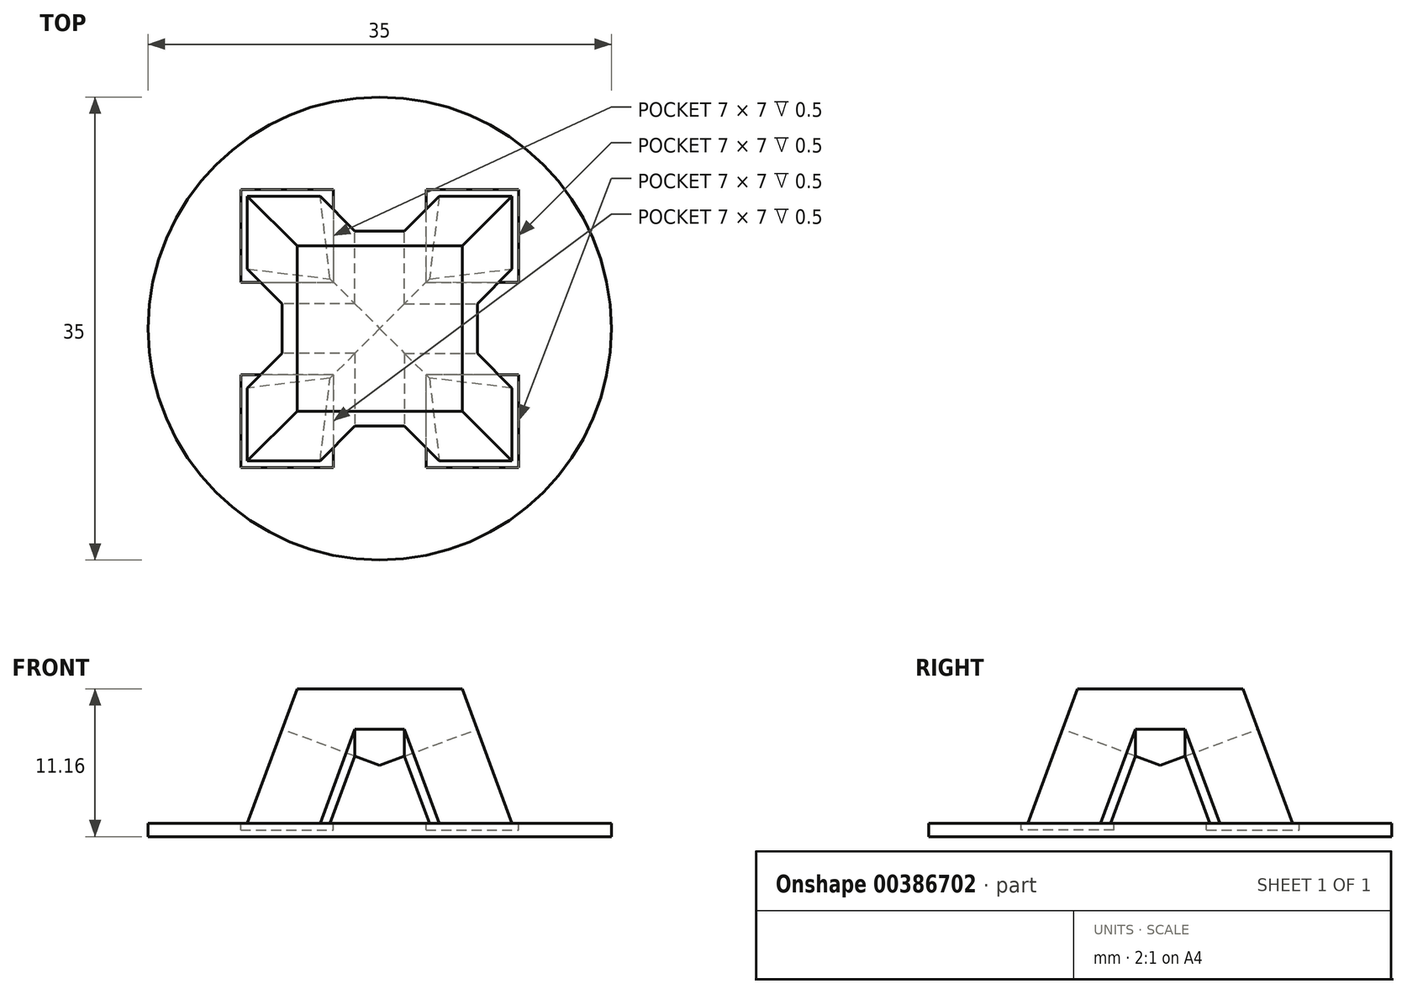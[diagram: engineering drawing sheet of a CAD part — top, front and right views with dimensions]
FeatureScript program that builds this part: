
annotation { "Feature Type Name" : "Feature", "Feature Type Description" : "" }
export const myFeature = defineFeature(function(context is Context, id is Id, definition is map)
    precondition{}
    {
        {
            var Q0;
            Q0=qCreatedBy(makeId("Top.planeOp"),FACE);
            var sketch = newSketch(context, id + "F0", { "sketchPlane" : qUnion([Q0])});
            skLineSegment(sketch, "E0.bottom", {"start": v(-10, 10) * mm, "end": v(10, 10) * mm});
            skLineSegment(sketch, "E0.top", {"start": v(-10, -10) * mm, "end": v(10, -10) * mm});
            skLineSegment(sketch, "E0.left", {"start": v(-10, 10) * mm, "end": v(-10, -10) * mm});
            skLineSegment(sketch, "E0.right", {"start": v(10, 10) * mm, "end": v(10, -10) * mm});
            skPoint(sketch, "E0.middle", {"position": v(0, 0) * mm});
            skSolve(sketch);
        }
        {
            var Q0;
            Q0=qCreatedBy(makeId("Top.planeOp"),FACE);
            cPlane(context, id + "F1", {"entities" : qUnion([Q0]), "cplaneType" : CPlaneType.OFFSET, "offset" : 10.16 * mm, "width" : 150 * mm, "height" : 150 * mm});
        }
        {
            var Q0;
            Q0=qCreatedBy(id+"F1.planeOp",FACE);
            var sketch = newSketch(context, id + "F2", { "sketchPlane" : qUnion([Q0])});
            skLineSegment(sketch, "E1.bottom", {"start": v(-6.25, 6.25) * mm, "end": v(6.25, 6.25) * mm});
            skLineSegment(sketch, "E1.top", {"start": v(-6.25, -6.25) * mm, "end": v(6.25, -6.25) * mm});
            skLineSegment(sketch, "E1.left", {"start": v(-6.25, 6.25) * mm, "end": v(-6.25, -6.25) * mm});
            skLineSegment(sketch, "E1.right", {"start": v(6.25, 6.25) * mm, "end": v(6.25, -6.25) * mm});
            skPoint(sketch, "E1.middle", {"position": v(0, 0) * mm});
            skSolve(sketch);
        }
        {
            var Q0;
            Q0=makeQuery(id+"F0.imprint","IMPRINT",FACE,{"disambiguationData":[TD([[makeQuery(id+"F0.imprint","IMPRINT",EDGE,{"derivedFrom":sQuery(id+"F0.wireOp",EDGE,"E0.bottom")}),-1.0]])]});
            var Q1;
            Q1=makeQuery(id+"F2.imprint","IMPRINT",FACE,{"disambiguationData":[TD([[makeQuery(id+"F2.imprint","IMPRINT",EDGE,{"derivedFrom":sQuery(id+"F2.wireOp",EDGE,"E1.bottom")}),-1.0]])]});
            loft(context, id + "F3", {"sheetProfilesArray" : [{ "sheetProfileEntities" : qUnion([Q0]) }, { "sheetProfileEntities" : qUnion([Q1]) }]});
        }
        {
            var Q0;
            Q0=makeQuery(id+"F3.opLoft","SWEPT_FACE",FACE,{"disambiguationData":[OSD([sQuery(id+"F0.wireOp",EDGE,"E0.top"),sQuery(id+"F0.wireOp",EDGE,"E0.left"),sQuery(id+"F0.wireOp",EDGE,"E0.right"),sQuery(id+"F2.wireOp",EDGE,"E1.top"),sQuery(id+"F2.wireOp",EDGE,"E1.left"),sQuery(id+"F2.wireOp",EDGE,"E1.right")])]});
            var sketch = newSketch(context, id + "F4", { "sketchPlane" : qUnion([Q0])});
            skLineSegment(sketch, "E2", {"start": v(-4.5, -3.46) * mm, "end": v(-1.88, 4.12) * mm});
            skLineSegment(sketch, "E3", {"start": v(-1.88, 4.12) * mm, "end": v(1.88, 4.12) * mm});
            skLineSegment(sketch, "E4", {"start": v(1.88, 4.12) * mm, "end": v(4.5, -3.46) * mm});
            skSolve(sketch);
        }
        {
            var Q0;
            Q0=makeQuery(id+"F3.opLoft","SWEPT_FACE",FACE,{"disambiguationData":[OSD([sQuery(id+"F0.wireOp",EDGE,"E0.bottom"),sQuery(id+"F0.wireOp",EDGE,"E0.top"),sQuery(id+"F0.wireOp",EDGE,"E0.right"),sQuery(id+"F2.wireOp",EDGE,"E1.bottom"),sQuery(id+"F2.wireOp",EDGE,"E1.top"),sQuery(id+"F2.wireOp",EDGE,"E1.right")])]});
            var sketch = newSketch(context, id + "F5", { "sketchPlane" : qUnion([Q0])});
            skLineSegment(sketch, "E5", {"start": v(-4.5, -3.46) * mm, "end": v(-1.88, 4.12) * mm});
            skLineSegment(sketch, "E6", {"start": v(-1.88, 4.12) * mm, "end": v(1.88, 4.12) * mm});
            skLineSegment(sketch, "E7", {"start": v(1.88, 4.12) * mm, "end": v(4.5, -3.46) * mm});
            skSolve(sketch);
        }
        {
            var Q0;
            Q0=makeQuery(id+"F3.opLoft","SWEPT_FACE",FACE,{"disambiguationData":[OSD([sQuery(id+"F0.wireOp",EDGE,"E0.bottom"),sQuery(id+"F0.wireOp",EDGE,"E0.left"),sQuery(id+"F0.wireOp",EDGE,"E0.right"),sQuery(id+"F2.wireOp",EDGE,"E1.bottom"),sQuery(id+"F2.wireOp",EDGE,"E1.left"),sQuery(id+"F2.wireOp",EDGE,"E1.right")])]});
            var sketch = newSketch(context, id + "F6", { "sketchPlane" : qUnion([Q0])});
            skLineSegment(sketch, "E8", {"start": v(-4.5, -3.46) * mm, "end": v(-1.88, 4.12) * mm});
            skLineSegment(sketch, "E9", {"start": v(-1.88, 4.12) * mm, "end": v(1.88, 4.12) * mm});
            skLineSegment(sketch, "E10", {"start": v(1.88, 4.12) * mm, "end": v(4.5, -3.46) * mm});
            skSolve(sketch);
        }
        {
            var Q0;
            Q0=makeQuery(id+"F3.opLoft","SWEPT_FACE",FACE,{"disambiguationData":[OSD([sQuery(id+"F0.wireOp",EDGE,"E0.bottom"),sQuery(id+"F0.wireOp",EDGE,"E0.top"),sQuery(id+"F0.wireOp",EDGE,"E0.left"),sQuery(id+"F2.wireOp",EDGE,"E1.bottom"),sQuery(id+"F2.wireOp",EDGE,"E1.top"),sQuery(id+"F2.wireOp",EDGE,"E1.left")])]});
            var sketch = newSketch(context, id + "F7", { "sketchPlane" : qUnion([Q0])});
            skLineSegment(sketch, "E11", {"start": v(-4.5, -3.46) * mm, "end": v(-1.88, 4.12) * mm});
            skLineSegment(sketch, "E12", {"start": v(-1.88, 4.12) * mm, "end": v(1.88, 4.12) * mm});
            skLineSegment(sketch, "E13", {"start": v(1.88, 4.12) * mm, "end": v(4.5, -3.46) * mm});
            skSolve(sketch);
        }
        {
            var Q0;
            {var subQ0=sQuery(id+"F7.wireOp",EDGE,"E11");Q0=makeQuery(id+"F7.imprint","IMPRINT",FACE,{"disambiguationData":[TD([[makeQuery(id+"F7.imprint","IMPRINT",EDGE,{"derivedFrom":subQ0}),-1.0]])]});}
            extrude(context, id + "F8", {"entities" : qUnion([Q0]), "operationType" : NewBodyOperationType.REMOVE, "oppositeDirection" : true, "depth" : 57.8 * mm});
        }
        {
            var Q0;
            {var subQ0=sQuery(id+"F4.wireOp",EDGE,"E2");Q0=makeQuery(id+"F4.imprint","IMPRINT",FACE,{"disambiguationData":[TD([[makeQuery(id+"F4.imprint","IMPRINT",EDGE,{"derivedFrom":subQ0}),-1.0]])]});}
            extrude(context, id + "F9", {"entities" : qUnion([Q0]), "operationType" : NewBodyOperationType.REMOVE, "oppositeDirection" : true, "depth" : 42.4 * mm});
        }
        {
            var Q0;
            {var subQ0=sQuery(id+"F6.wireOp",EDGE,"E8");Q0=makeQuery(id+"F6.imprint","IMPRINT",FACE,{"disambiguationData":[TD([[makeQuery(id+"F6.imprint","IMPRINT",EDGE,{"derivedFrom":subQ0}),-1.0]])]});}
            extrude(context, id + "F10", {"entities" : qUnion([Q0]), "operationType" : NewBodyOperationType.REMOVE, "oppositeDirection" : true, "depth" : 44.5 * mm});
        }
        {
            var Q0;
            {var subQ0=sQuery(id+"F5.wireOp",EDGE,"E5");Q0=makeQuery(id+"F5.imprint","IMPRINT",FACE,{"disambiguationData":[TD([[makeQuery(id+"F5.imprint","IMPRINT",EDGE,{"derivedFrom":subQ0}),-1.0]])]});}
            extrude(context, id + "F11", {"entities" : qUnion([Q0]), "operationType" : NewBodyOperationType.REMOVE, "oppositeDirection" : true, "depth" : 38.1 * mm});
        }
        {
            var Q0;
            Q0=qCreatedBy(makeId("Top.planeOp"),FACE);
            var sketch = newSketch(context, id + "F12", { "sketchPlane" : qUnion([Q0])});
            skCircle(sketch, "E14", {"center": v(0, 0) * mm, "radius": 17.5 * mm});
            skSolve(sketch);
        }
        {
            var Q0;
            Q0=makeQuery(id+"F12.imprint","IMPRINT",FACE,{"disambiguationData":[TD([[makeQuery(id+"F12.imprint","IMPRINT",EDGE,{"derivedFrom":sQuery(id+"F12.wireOp",EDGE,"E14")}),1.0]])]});
            extrude(context, id + "F13", {"entities" : qUnion([Q0]), "oppositeDirection" : true, "depth" : 1 * mm});
        }
        {
            var Q0;
            Q0=makeQuery(id+"F13.opExtrude","CAP_FACE",FACE,{"disambiguationData":[OSD([sQuery(id+"F12.wireOp",EDGE,"E14")])],"isStart":true});
            var sketch = newSketch(context, id + "F14", { "sketchPlane" : qUnion([Q0])});
            skLineSegment(sketch, "E15", {"start": v(0, 19.01) * mm, "end": v(0, -18.83) * mm, "construction": true});
            skLineSegment(sketch, "E16", {"start": v(-19.93, 0) * mm, "end": v(20.99, 0) * mm, "construction": true});
            skLineSegment(sketch, "E17", {"start": v(10.5, 14) * mm, "end": v(10.5, -14) * mm});
            skLineSegment(sketch, "E18", {"start": v(-10.5, -14) * mm, "end": v(-10.5, 14) * mm});
            skLineSegment(sketch, "E19", {"start": v(-14, 10.5) * mm, "end": v(14, 10.5) * mm});
            skLineSegment(sketch, "E20", {"start": v(14, -10.5) * mm, "end": v(-14, -10.5) * mm});
            skLineSegment(sketch, "E21", {"start": v(-17.15, 3.5) * mm, "end": v(17.15, 3.5) * mm});
            skLineSegment(sketch, "E22", {"start": v(17.15, -3.5) * mm, "end": v(-17.15, -3.5) * mm});
            skLineSegment(sketch, "E23", {"start": v(-3.5, 17.15) * mm, "end": v(-3.5, -17.15) * mm});
            skLineSegment(sketch, "E24", {"start": v(3.5, -17.15) * mm, "end": v(3.5, 17.15) * mm});
            skSolve(sketch);
        }
        {
            var Q0;
            {var subQ0=sQuery(id+"F14.wireOp",EDGE,"E21");var subQ1=sQuery(id+"F14.wireOp",EDGE,"E18");var subQ2=makeQuery(id+"F14.imprint","INTERSECT",VERTEX,{"derivedFrom":[subQ1,subQ0]});Q0=makeQuery(id+"F14.imprint","IMPRINT",FACE,{"disambiguationData":[TD([[makeQuery(id+"F14.imprint","IMPRINT",EDGE,{"disambiguationData":[TD([[subQ2,-1.0]])],"derivedFrom":subQ1}),-1.0]])]});}
            var Q1;
            {var subQ0=sQuery(id+"F14.wireOp",EDGE,"E19");var subQ1=sQuery(id+"F14.wireOp",EDGE,"E17");var subQ2=makeQuery(id+"F14.imprint","INTERSECT",VERTEX,{"derivedFrom":[subQ1,subQ0]});Q1=makeQuery(id+"F14.imprint","IMPRINT",FACE,{"disambiguationData":[TD([[makeQuery(id+"F14.imprint","IMPRINT",EDGE,{"disambiguationData":[TD([[subQ2,-1.0]])],"derivedFrom":subQ1}),-1.0]])]});}
            var Q2;
            {var subQ0=sQuery(id+"F14.wireOp",EDGE,"E22");var subQ1=sQuery(id+"F14.wireOp",EDGE,"E17");var subQ2=makeQuery(id+"F14.imprint","INTERSECT",VERTEX,{"derivedFrom":[subQ1,subQ0]});Q2=makeQuery(id+"F14.imprint","IMPRINT",FACE,{"disambiguationData":[TD([[makeQuery(id+"F14.imprint","IMPRINT",EDGE,{"disambiguationData":[TD([[subQ2,-1.0]])],"derivedFrom":subQ1}),-1.0]])]});}
            var Q3;
            {var subQ0=sQuery(id+"F14.wireOp",EDGE,"E20");var subQ1=sQuery(id+"F14.wireOp",EDGE,"E18");var subQ2=makeQuery(id+"F14.imprint","INTERSECT",VERTEX,{"derivedFrom":[subQ1,subQ0]});Q3=makeQuery(id+"F14.imprint","IMPRINT",FACE,{"disambiguationData":[TD([[makeQuery(id+"F14.imprint","IMPRINT",EDGE,{"disambiguationData":[TD([[subQ2,-1.0]])],"derivedFrom":subQ1}),-1.0]])]});}
            extrude(context, id + "F15", {"entities" : qUnion([Q0, Q1, Q2, Q3]), "operationType" : NewBodyOperationType.REMOVE, "oppositeDirection" : true, "depth" : .5 * mm});
        }
    });
